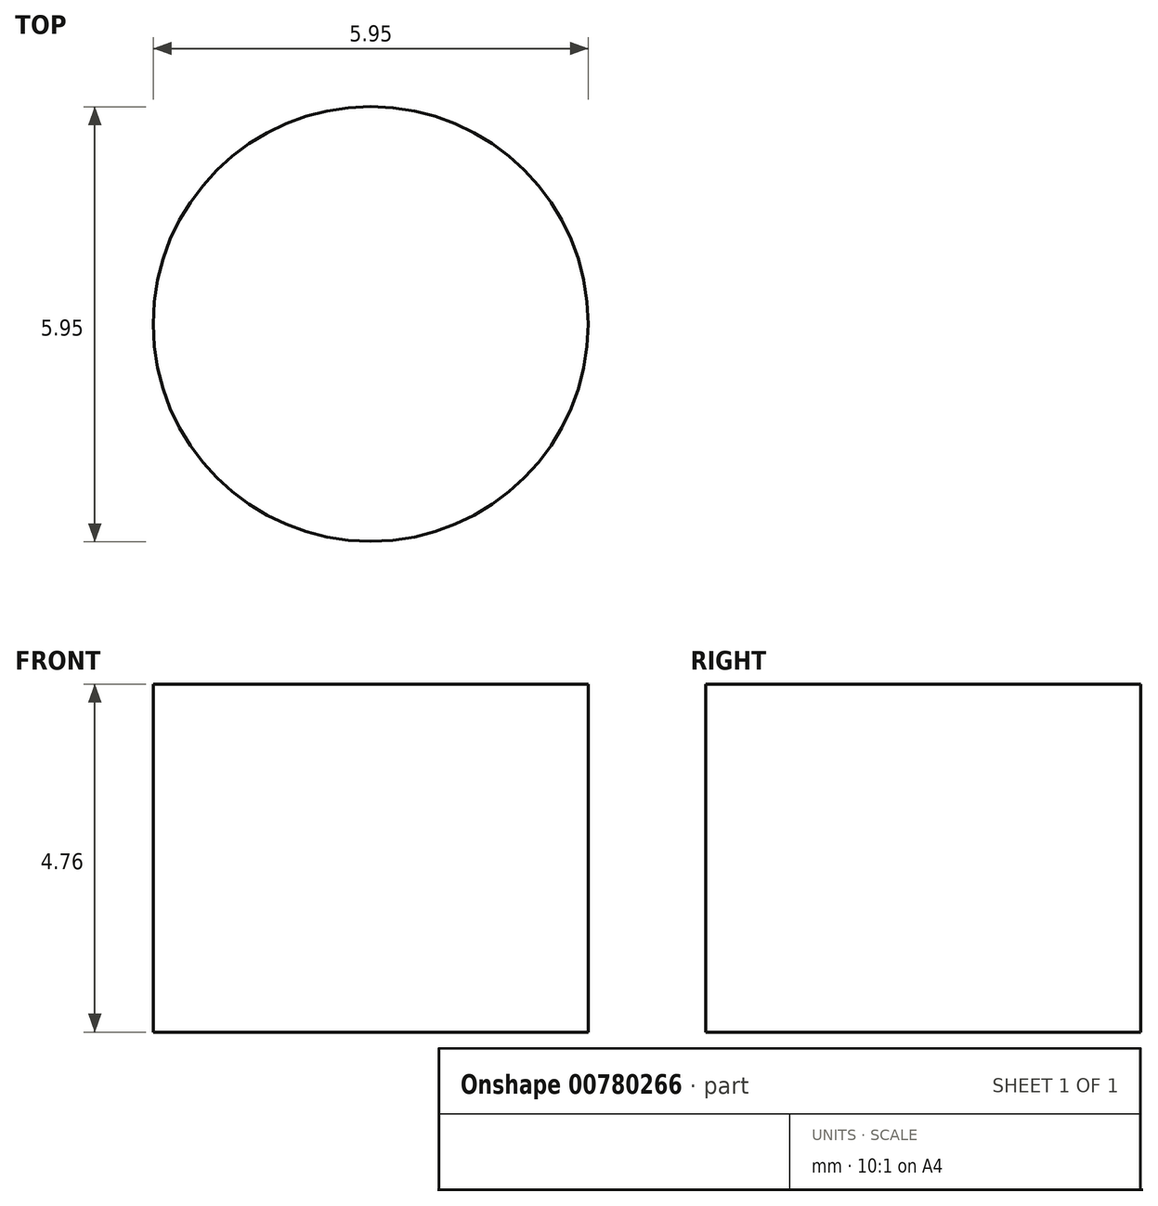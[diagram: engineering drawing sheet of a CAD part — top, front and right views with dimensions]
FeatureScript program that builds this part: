
annotation { "Feature Type Name" : "Feature", "Feature Type Description" : "" }
export const myFeature = defineFeature(function(context is Context, id is Id, definition is map)
    precondition{}
    {
        {
            var Q0;
            Q0=qCreatedBy(makeId("Top.planeOp"),FACE);
            var sketch = newSketch(context, id + "F0", { "sketchPlane" : qUnion([Q0])});
            skCircle(sketch, "E0", {"center": v(-141.6, -26.75) * mm, "radius": 2.98 * mm});
            skSolve(sketch);
        }
        {
            var Q0;
            Q0 = qSketchRegion(id + "F0", true);
            extrude(context, id + "F1", {"entities" : qUnion([Q0]), "depth" : 4.76 * mm, "offsetDistance" : 25 * mm});
        }
    });
